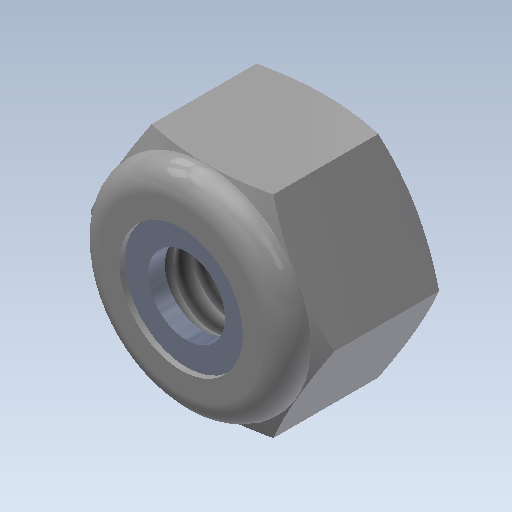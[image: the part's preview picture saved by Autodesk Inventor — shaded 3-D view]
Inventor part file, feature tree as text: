
AUTODESK INVENTOR PART (.ipt)
format: ipt  version: 2020 (Build 240168000, 168)  size: 233,984 bytes
history: native  units: in
note: dims shown in document units (in); Inventor stores cm internally (conversion verified against a paired STEP export)
features: sketch x5, extrude x2, revolve x2, projected_geometry x2, hole x1
ambient origin geometry x8: Origin, YZ Plane, XZ Plane, XY Plane, X Axis, Y Axis, Z Axis, Center Point
bodies: Solid1 (feature_tree)
feature tree (12):
  extrude  "Extrusion1"  Depth=0.195in TaperAngle=0.0deg
  revolve  "Revolution1"  [1 undecoded]
  revolve  "Revolution2"  Angle=90.0deg
  hole  "Hole1"  [1 undecoded]
  extrude  "Extrusion2"  Depth=0.027in
  sketch  "Sketch1"  dims[d0=0.3438in d1=0.195in d2=0.0in]
  sketch  "Sketch2"  dims[d5=0.039in d6=0.039in]
  sketch  "Sketch3"  dims[d7=0.133in d8=90.0deg]
  sketch  "Sketch4"  dims[d9=0.027in d10=0.012in]
  sketch  "Sketch5"  dims[d11=0.012in d12=0.027in d13=90.0deg d14=0.13in d15=0.75in d16=0.201in d17=0.009in d18=0.5635in d19=1.0in d20=0.8108in d21=0.125in d24=0.027in d25=0.0in]
  projected_geometry  "Project Cut Edges1"
  projected_geometry  "Project Cut Edges2"
note: 2 required parameter values undecoded (feature->parameter linkage not recoverable at this tier; creation-order binding heuristic only, values carry confidence <= 0.55)